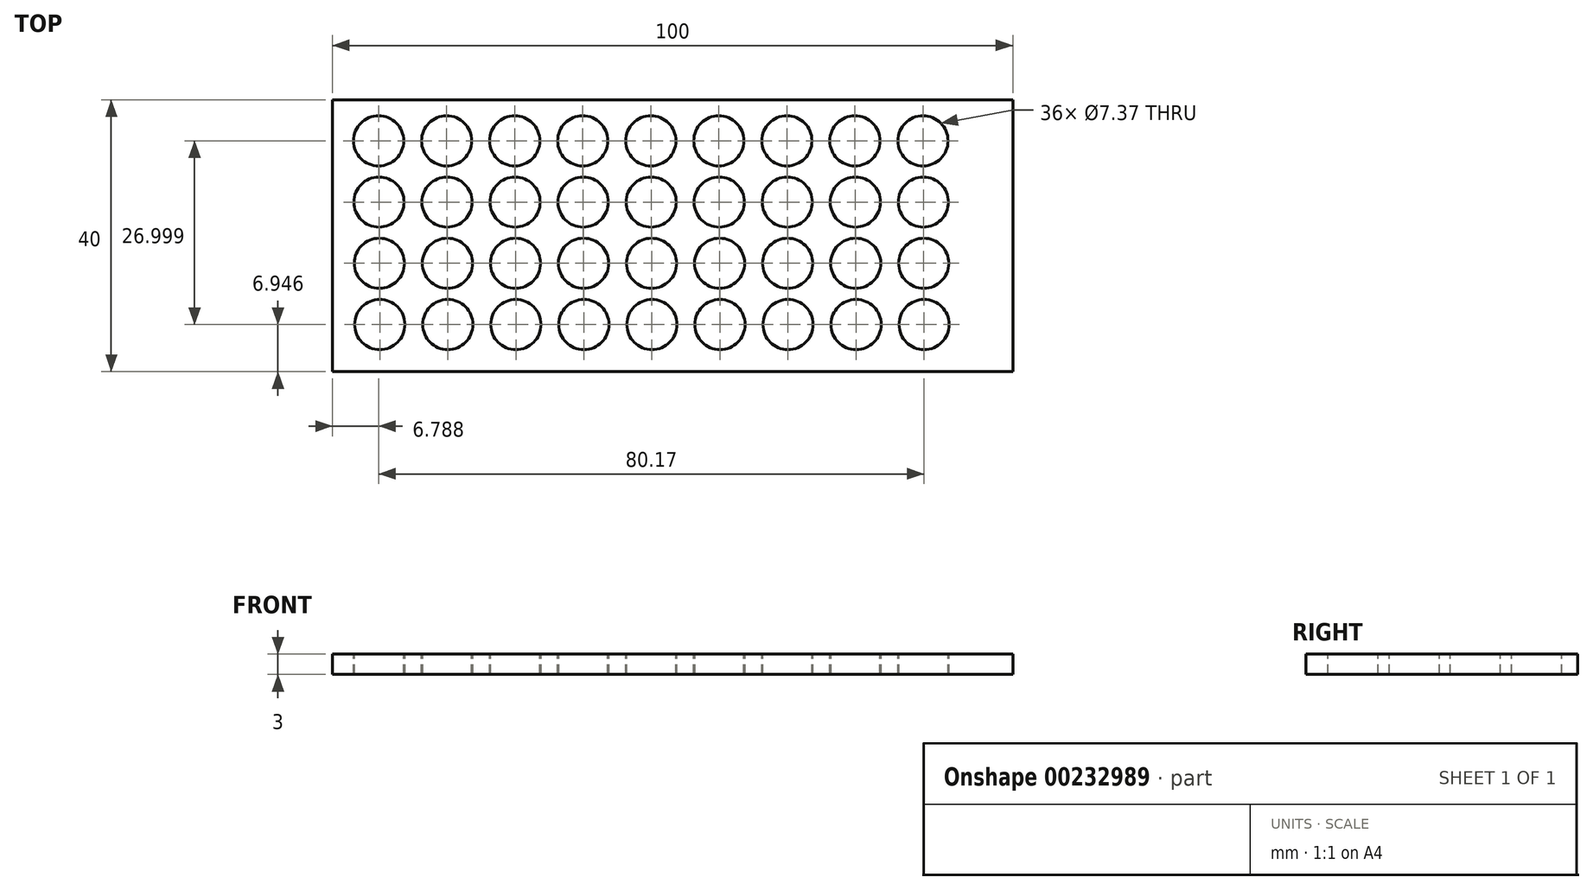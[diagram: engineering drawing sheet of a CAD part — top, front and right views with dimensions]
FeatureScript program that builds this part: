
annotation { "Feature Type Name" : "Feature", "Feature Type Description" : "" }
export const myFeature = defineFeature(function(context is Context, id is Id, definition is map)
    precondition{}
    {
        {
            var Q0;
            Q0=qCreatedBy(makeId("Top.planeOp"),FACE);
            var sketch = newSketch(context, id + "F0", { "sketchPlane" : qUnion([Q0])});
            skLineSegment(sketch, "E0.bottom", {"start": v(-50, 20) * mm, "end": v(50, 20) * mm});
            skLineSegment(sketch, "E0.top", {"start": v(-50, -20) * mm, "end": v(50, -20) * mm});
            skLineSegment(sketch, "E0.left", {"start": v(-50, 20) * mm, "end": v(-50, -20) * mm});
            skLineSegment(sketch, "E0.right", {"start": v(50, 20) * mm, "end": v(50, -20) * mm});
            skSolve(sketch);
        }
        {
            var Q0;
            Q0 = qSketchRegion(id + "F0", true);
            extrude(context, id + "F1", {"entities" : qUnion([Q0]), "depth" : 3 * mm});
        }
        {
            var Q0;
            Q0=makeQuery(id+"F1.opExtrude","CAP_FACE",FACE,{"disambiguationData":[OSD([sQuery(id+"F0.wireOp",EDGE,"E0.bottom"),sQuery(id+"F0.wireOp",EDGE,"E0.top"),sQuery(id+"F0.wireOp",EDGE,"E0.left"),sQuery(id+"F0.wireOp",EDGE,"E0.right")])],"isStart":false});
            var sketch = newSketch(context, id + "F2", { "sketchPlane" : qUnion([Q0])});
            skCircle(sketch, "E1", {"center": v(-43.04, -13.05) * mm, "radius": 3.69 * mm});
            skCircle(sketch, "E2.0.1.0", {"center": v(-43.1, -4.05) * mm, "radius": 3.69 * mm});
            skCircle(sketch, "E2.0.2.0", {"center": v(-43.16, 4.95) * mm, "radius": 3.69 * mm});
            skCircle(sketch, "E2.0.3.0", {"center": v(-43.21, 13.95) * mm, "radius": 3.69 * mm});
            skCircle(sketch, "E2.1.0.0", {"center": v(-33.04, -13.05) * mm, "radius": 3.69 * mm});
            skCircle(sketch, "E2.1.1.0", {"center": v(-33.1, -4.05) * mm, "radius": 3.69 * mm});
            skCircle(sketch, "E2.1.2.0", {"center": v(-33.16, 4.95) * mm, "radius": 3.69 * mm});
            skCircle(sketch, "E2.1.3.0", {"center": v(-33.21, 13.95) * mm, "radius": 3.69 * mm});
            skCircle(sketch, "E2.2.0.0", {"center": v(-23.04, -13.05) * mm, "radius": 3.69 * mm});
            skCircle(sketch, "E2.2.1.0", {"center": v(-23.1, -4.05) * mm, "radius": 3.69 * mm});
            skCircle(sketch, "E2.2.2.0", {"center": v(-23.16, 4.95) * mm, "radius": 3.69 * mm});
            skCircle(sketch, "E2.2.3.0", {"center": v(-23.21, 13.95) * mm, "radius": 3.69 * mm});
            skCircle(sketch, "E2.3.0.0", {"center": v(-13.04, -13.05) * mm, "radius": 3.69 * mm});
            skCircle(sketch, "E2.3.1.0", {"center": v(-13.1, -4.05) * mm, "radius": 3.69 * mm});
            skCircle(sketch, "E2.3.2.0", {"center": v(-13.16, 4.95) * mm, "radius": 3.69 * mm});
            skCircle(sketch, "E2.3.3.0", {"center": v(-13.21, 13.95) * mm, "radius": 3.69 * mm});
            skCircle(sketch, "E2.4.0.0", {"center": v(-3.04, -13.05) * mm, "radius": 3.69 * mm});
            skCircle(sketch, "E2.4.1.0", {"center": v(-3.1, -4.05) * mm, "radius": 3.69 * mm});
            skCircle(sketch, "E2.4.2.0", {"center": v(-3.16, 4.95) * mm, "radius": 3.69 * mm});
            skCircle(sketch, "E2.4.3.0", {"center": v(-3.21, 13.95) * mm, "radius": 3.69 * mm});
            skCircle(sketch, "E2.5.0.0", {"center": v(6.96, -13.05) * mm, "radius": 3.69 * mm});
            skCircle(sketch, "E2.5.1.0", {"center": v(6.9, -4.05) * mm, "radius": 3.69 * mm});
            skCircle(sketch, "E2.5.2.0", {"center": v(6.84, 4.95) * mm, "radius": 3.69 * mm});
            skCircle(sketch, "E2.5.3.0", {"center": v(6.79, 13.95) * mm, "radius": 3.69 * mm});
            skCircle(sketch, "E2.6.0.0", {"center": v(16.96, -13.05) * mm, "radius": 3.69 * mm});
            skCircle(sketch, "E2.6.1.0", {"center": v(16.9, -4.05) * mm, "radius": 3.69 * mm});
            skCircle(sketch, "E2.6.2.0", {"center": v(16.84, 4.95) * mm, "radius": 3.69 * mm});
            skCircle(sketch, "E2.6.3.0", {"center": v(16.79, 13.95) * mm, "radius": 3.69 * mm});
            skCircle(sketch, "E2.7.0.0", {"center": v(26.96, -13.05) * mm, "radius": 3.69 * mm});
            skCircle(sketch, "E2.7.1.0", {"center": v(26.9, -4.05) * mm, "radius": 3.69 * mm});
            skCircle(sketch, "E2.7.2.0", {"center": v(26.84, 4.95) * mm, "radius": 3.69 * mm});
            skCircle(sketch, "E2.7.3.0", {"center": v(26.79, 13.95) * mm, "radius": 3.69 * mm});
            skCircle(sketch, "E2.8.0.0", {"center": v(36.96, -13.05) * mm, "radius": 3.69 * mm});
            skCircle(sketch, "E2.8.1.0", {"center": v(36.9, -4.05) * mm, "radius": 3.69 * mm});
            skCircle(sketch, "E2.8.2.0", {"center": v(36.84, 4.95) * mm, "radius": 3.69 * mm});
            skCircle(sketch, "E2.8.3.0", {"center": v(36.79, 13.95) * mm, "radius": 3.69 * mm});
            skLineSegment(sketch, "E2.direction1", {"start": v(-43.04, -13.05) * mm, "end": v(-33.04, -13.05) * mm, "construction": true});
            skLineSegment(sketch, "E2.direction2", {"start": v(-43.04, -13.05) * mm, "end": v(-43.1, -4.05) * mm, "construction": true});
            skSolve(sketch);
        }
        {
            var Q0;
            Q0=makeQuery(id+"F2.imprint","IMPRINT",FACE,{"disambiguationData":[TD([[makeQuery(id+"F2.imprint","IMPRINT",EDGE,{"derivedFrom":sQuery(id+"F2.wireOp",EDGE,"E1")}),1.0]])]});
            var Q1;
            Q1=makeQuery(id+"F2.imprint","IMPRINT",FACE,{"disambiguationData":[TD([[makeQuery(id+"F2.imprint","IMPRINT",EDGE,{"derivedFrom":sQuery(id+"F2.wireOp",EDGE,"E2.0.1.0")}),1.0]])]});
            var Q2;
            Q2=makeQuery(id+"F2.imprint","IMPRINT",FACE,{"disambiguationData":[TD([[makeQuery(id+"F2.imprint","IMPRINT",EDGE,{"derivedFrom":sQuery(id+"F2.wireOp",EDGE,"E2.0.2.0")}),1.0]])]});
            var Q3;
            Q3=makeQuery(id+"F2.imprint","IMPRINT",FACE,{"disambiguationData":[TD([[makeQuery(id+"F2.imprint","IMPRINT",EDGE,{"derivedFrom":sQuery(id+"F2.wireOp",EDGE,"E2.0.3.0")}),1.0]])]});
            var Q4;
            Q4=makeQuery(id+"F2.imprint","IMPRINT",FACE,{"disambiguationData":[TD([[makeQuery(id+"F2.imprint","IMPRINT",EDGE,{"derivedFrom":sQuery(id+"F2.wireOp",EDGE,"E2.1.2.0")}),1.0]])]});
            var Q5;
            Q5=makeQuery(id+"F2.imprint","IMPRINT",FACE,{"disambiguationData":[TD([[makeQuery(id+"F2.imprint","IMPRINT",EDGE,{"derivedFrom":sQuery(id+"F2.wireOp",EDGE,"E2.1.3.0")}),1.0]])]});
            var Q6;
            Q6=makeQuery(id+"F2.imprint","IMPRINT",FACE,{"disambiguationData":[TD([[makeQuery(id+"F2.imprint","IMPRINT",EDGE,{"derivedFrom":sQuery(id+"F2.wireOp",EDGE,"E2.1.1.0")}),1.0]])]});
            var Q7;
            Q7=makeQuery(id+"F2.imprint","IMPRINT",FACE,{"disambiguationData":[TD([[makeQuery(id+"F2.imprint","IMPRINT",EDGE,{"derivedFrom":sQuery(id+"F2.wireOp",EDGE,"E2.1.0.0")}),1.0]])]});
            var Q8;
            Q8=makeQuery(id+"F2.imprint","IMPRINT",FACE,{"disambiguationData":[TD([[makeQuery(id+"F2.imprint","IMPRINT",EDGE,{"derivedFrom":sQuery(id+"F2.wireOp",EDGE,"E2.2.0.0")}),1.0]])]});
            var Q9;
            Q9=makeQuery(id+"F2.imprint","IMPRINT",FACE,{"disambiguationData":[TD([[makeQuery(id+"F2.imprint","IMPRINT",EDGE,{"derivedFrom":sQuery(id+"F2.wireOp",EDGE,"E2.2.1.0")}),1.0]])]});
            var Q10;
            Q10=makeQuery(id+"F2.imprint","IMPRINT",FACE,{"disambiguationData":[TD([[makeQuery(id+"F2.imprint","IMPRINT",EDGE,{"derivedFrom":sQuery(id+"F2.wireOp",EDGE,"E2.2.3.0")}),1.0]])]});
            var Q11;
            Q11=makeQuery(id+"F2.imprint","IMPRINT",FACE,{"disambiguationData":[TD([[makeQuery(id+"F2.imprint","IMPRINT",EDGE,{"derivedFrom":sQuery(id+"F2.wireOp",EDGE,"E2.2.2.0")}),1.0]])]});
            var Q12;
            Q12=makeQuery(id+"F2.imprint","IMPRINT",FACE,{"disambiguationData":[TD([[makeQuery(id+"F2.imprint","IMPRINT",EDGE,{"derivedFrom":sQuery(id+"F2.wireOp",EDGE,"E2.3.1.0")}),1.0]])]});
            var Q13;
            Q13=makeQuery(id+"F2.imprint","IMPRINT",FACE,{"disambiguationData":[TD([[makeQuery(id+"F2.imprint","IMPRINT",EDGE,{"derivedFrom":sQuery(id+"F2.wireOp",EDGE,"E2.3.0.0")}),1.0]])]});
            var Q14;
            Q14=makeQuery(id+"F2.imprint","IMPRINT",FACE,{"disambiguationData":[TD([[makeQuery(id+"F2.imprint","IMPRINT",EDGE,{"derivedFrom":sQuery(id+"F2.wireOp",EDGE,"E2.4.0.0")}),1.0]])]});
            var Q15;
            Q15=makeQuery(id+"F2.imprint","IMPRINT",FACE,{"disambiguationData":[TD([[makeQuery(id+"F2.imprint","IMPRINT",EDGE,{"derivedFrom":sQuery(id+"F2.wireOp",EDGE,"E2.4.1.0")}),1.0]])]});
            var Q16;
            Q16=makeQuery(id+"F2.imprint","IMPRINT",FACE,{"disambiguationData":[TD([[makeQuery(id+"F2.imprint","IMPRINT",EDGE,{"derivedFrom":sQuery(id+"F2.wireOp",EDGE,"E2.3.2.0")}),1.0]])]});
            var Q17;
            Q17=makeQuery(id+"F2.imprint","IMPRINT",FACE,{"disambiguationData":[TD([[makeQuery(id+"F2.imprint","IMPRINT",EDGE,{"derivedFrom":sQuery(id+"F2.wireOp",EDGE,"E2.3.3.0")}),1.0]])]});
            var Q18;
            Q18=makeQuery(id+"F2.imprint","IMPRINT",FACE,{"disambiguationData":[TD([[makeQuery(id+"F2.imprint","IMPRINT",EDGE,{"derivedFrom":sQuery(id+"F2.wireOp",EDGE,"E2.4.3.0")}),1.0]])]});
            var Q19;
            Q19=makeQuery(id+"F2.imprint","IMPRINT",FACE,{"disambiguationData":[TD([[makeQuery(id+"F2.imprint","IMPRINT",EDGE,{"derivedFrom":sQuery(id+"F2.wireOp",EDGE,"E2.4.2.0")}),1.0]])]});
            var Q20;
            Q20=makeQuery(id+"F2.imprint","IMPRINT",FACE,{"disambiguationData":[TD([[makeQuery(id+"F2.imprint","IMPRINT",EDGE,{"derivedFrom":sQuery(id+"F2.wireOp",EDGE,"E2.5.0.0")}),1.0]])]});
            var Q21;
            Q21=makeQuery(id+"F2.imprint","IMPRINT",FACE,{"disambiguationData":[TD([[makeQuery(id+"F2.imprint","IMPRINT",EDGE,{"derivedFrom":sQuery(id+"F2.wireOp",EDGE,"E2.5.1.0")}),1.0]])]});
            var Q22;
            Q22=makeQuery(id+"F2.imprint","IMPRINT",FACE,{"disambiguationData":[TD([[makeQuery(id+"F2.imprint","IMPRINT",EDGE,{"derivedFrom":sQuery(id+"F2.wireOp",EDGE,"E2.5.2.0")}),1.0]])]});
            var Q23;
            Q23=makeQuery(id+"F2.imprint","IMPRINT",FACE,{"disambiguationData":[TD([[makeQuery(id+"F2.imprint","IMPRINT",EDGE,{"derivedFrom":sQuery(id+"F2.wireOp",EDGE,"E2.5.3.0")}),1.0]])]});
            var Q24;
            Q24=makeQuery(id+"F2.imprint","IMPRINT",FACE,{"disambiguationData":[TD([[makeQuery(id+"F2.imprint","IMPRINT",EDGE,{"derivedFrom":sQuery(id+"F2.wireOp",EDGE,"E2.6.0.0")}),1.0]])]});
            var Q25;
            Q25=makeQuery(id+"F2.imprint","IMPRINT",FACE,{"disambiguationData":[TD([[makeQuery(id+"F2.imprint","IMPRINT",EDGE,{"derivedFrom":sQuery(id+"F2.wireOp",EDGE,"E2.6.1.0")}),1.0]])]});
            var Q26;
            Q26=makeQuery(id+"F2.imprint","IMPRINT",FACE,{"disambiguationData":[TD([[makeQuery(id+"F2.imprint","IMPRINT",EDGE,{"derivedFrom":sQuery(id+"F2.wireOp",EDGE,"E2.6.2.0")}),1.0]])]});
            var Q27;
            Q27=makeQuery(id+"F2.imprint","IMPRINT",FACE,{"disambiguationData":[TD([[makeQuery(id+"F2.imprint","IMPRINT",EDGE,{"derivedFrom":sQuery(id+"F2.wireOp",EDGE,"E2.6.3.0")}),1.0]])]});
            var Q28;
            Q28=makeQuery(id+"F2.imprint","IMPRINT",FACE,{"disambiguationData":[TD([[makeQuery(id+"F2.imprint","IMPRINT",EDGE,{"derivedFrom":sQuery(id+"F2.wireOp",EDGE,"E2.7.0.0")}),1.0]])]});
            var Q29;
            Q29=makeQuery(id+"F2.imprint","IMPRINT",FACE,{"disambiguationData":[TD([[makeQuery(id+"F2.imprint","IMPRINT",EDGE,{"derivedFrom":sQuery(id+"F2.wireOp",EDGE,"E2.7.1.0")}),1.0]])]});
            var Q30;
            Q30=makeQuery(id+"F2.imprint","IMPRINT",FACE,{"disambiguationData":[TD([[makeQuery(id+"F2.imprint","IMPRINT",EDGE,{"derivedFrom":sQuery(id+"F2.wireOp",EDGE,"E2.7.2.0")}),1.0]])]});
            var Q31;
            Q31=makeQuery(id+"F2.imprint","IMPRINT",FACE,{"disambiguationData":[TD([[makeQuery(id+"F2.imprint","IMPRINT",EDGE,{"derivedFrom":sQuery(id+"F2.wireOp",EDGE,"E2.8.1.0")}),1.0]])]});
            var Q32;
            Q32=makeQuery(id+"F2.imprint","IMPRINT",FACE,{"disambiguationData":[TD([[makeQuery(id+"F2.imprint","IMPRINT",EDGE,{"derivedFrom":sQuery(id+"F2.wireOp",EDGE,"E2.8.0.0")}),1.0]])]});
            var Q33;
            Q33=makeQuery(id+"F2.imprint","IMPRINT",FACE,{"disambiguationData":[TD([[makeQuery(id+"F2.imprint","IMPRINT",EDGE,{"derivedFrom":sQuery(id+"F2.wireOp",EDGE,"E2.8.2.0")}),1.0]])]});
            var Q34;
            Q34=makeQuery(id+"F2.imprint","IMPRINT",FACE,{"disambiguationData":[TD([[makeQuery(id+"F2.imprint","IMPRINT",EDGE,{"derivedFrom":sQuery(id+"F2.wireOp",EDGE,"E2.8.3.0")}),1.0]])]});
            var Q35;
            Q35=makeQuery(id+"F2.imprint","IMPRINT",FACE,{"disambiguationData":[TD([[makeQuery(id+"F2.imprint","IMPRINT",EDGE,{"derivedFrom":sQuery(id+"F2.wireOp",EDGE,"E2.7.3.0")}),1.0]])]});
            extrude(context, id + "F3", {"entities" : qUnion([Q0, Q1, Q2, Q3, Q4, Q5, Q6, Q7, Q8, Q9, Q10, Q11, Q12, Q13, Q14, Q15, Q16, Q17, Q18, Q19, Q20, Q21, Q22, Q23, Q24, Q25, Q26, Q27, Q28, Q29, Q30, Q31, Q32, Q33, Q34, Q35]), "operationType" : NewBodyOperationType.REMOVE, "oppositeDirection" : true, "depth" : 25 * mm});
        }
    });
